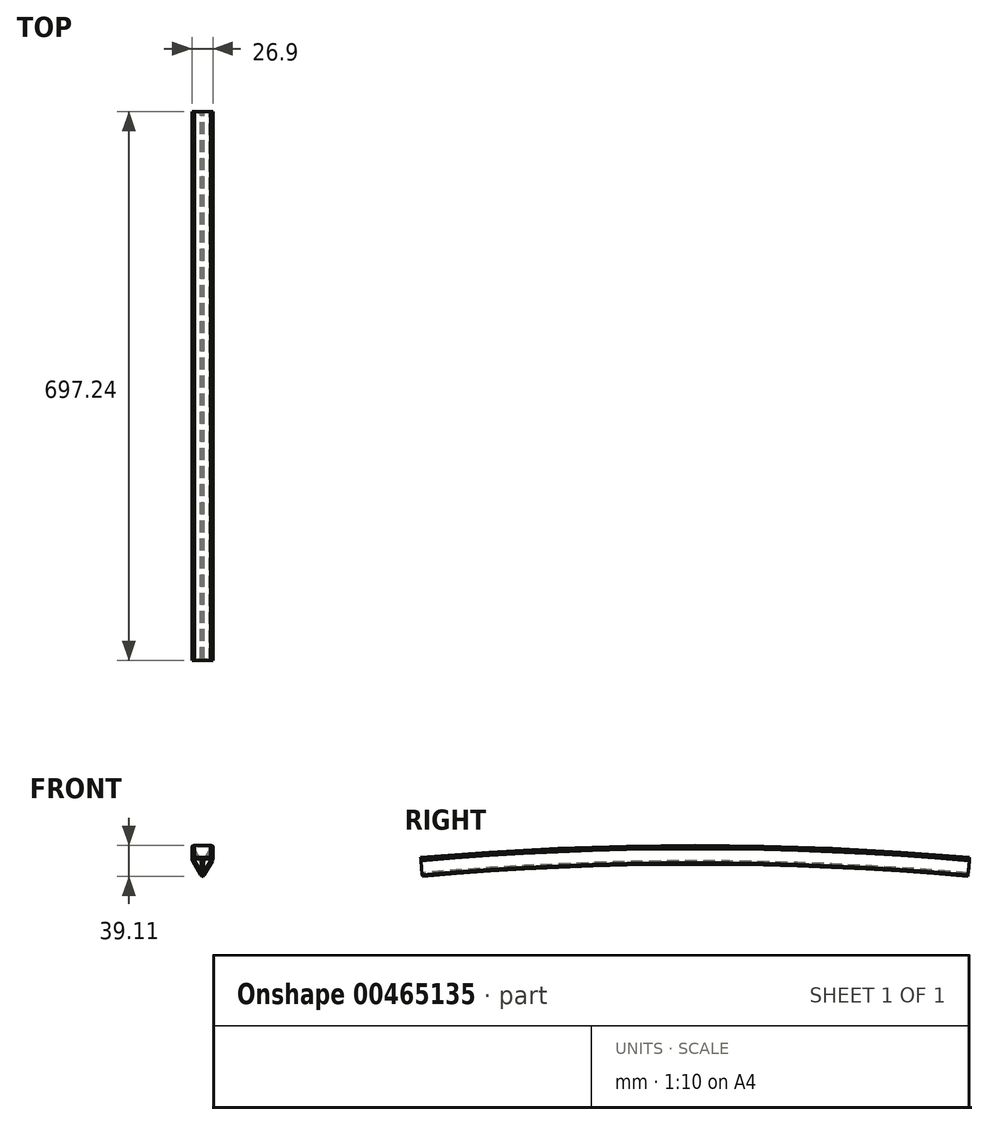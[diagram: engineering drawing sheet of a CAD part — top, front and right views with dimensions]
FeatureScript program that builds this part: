
annotation { "Feature Type Name" : "Feature", "Feature Type Description" : "" }
export const myFeature = defineFeature(function(context is Context, id is Id, definition is map)
    precondition{}
    {
        {
            var Q0;
            Q0=qCreatedBy(makeId("Front.planeOp"),FACE);
            var sketch = newSketch(context, id + "F0", { "sketchPlane" : qUnion([Q0])});
            skLineSegment(sketch, "E0", {"start": v(-10.27, 9) * mm, "end": v(10.27, 9) * mm});
            skLineSegment(sketch, "E1", {"start": v(12.63, 4.9) * mm, "end": v(2.37, -12.88) * mm});
            skLineSegment(sketch, "E2", {"start": v(-2.37, -12.88) * mm, "end": v(-12.63, 4.9) * mm});
            skPoint(sketch, "E3", {"position": v(0, 9) * mm});
            skPoint(sketch, "E4", {"position": v(7.5, -4) * mm});
            skPoint(sketch, "E5", {"position": v(-7.5, -4) * mm});
            skLineSegment(sketch, "E6", {"start": v(0, -14.98) * mm, "end": v(0.68, -14.8) * mm});
            skPoint(sketch, "E7", {"position": v(0.68, -14.8) * mm});
            skLineSegment(sketch, "E8", {"start": v(0.68, -14.8) * mm, "end": v(1.2, -14.4) * mm});
            skPoint(sketch, "E9", {"position": v(1.2, -14.4) * mm});
            skLineSegment(sketch, "E10", {"start": v(1.2, -14.4) * mm, "end": v(1.62, -13.92) * mm});
            skPoint(sketch, "E11", {"position": v(1.62, -13.92) * mm});
            skLineSegment(sketch, "E12", {"start": v(1.62, -13.92) * mm, "end": v(2.37, -12.88) * mm});
            skLineSegment(sketch, "E13.MirrorCS", {"start": v(-0.68, -14.8) * mm, "end": v(-1.2, -14.4) * mm});
            skLineSegment(sketch, "E14.MirrorCS", {"start": v(-1.2, -14.4) * mm, "end": v(-1.62, -13.92) * mm});
            skLineSegment(sketch, "E15.MirrorCS", {"start": v(-1.62, -13.92) * mm, "end": v(-2.37, -12.88) * mm});
            skLineSegment(sketch, "E16.MirrorCS", {"start": v(0, -14.98) * mm, "end": v(-0.68, -14.8) * mm});
            skLineSegment(sketch, "E17.MirrorCS", {"start": v(13.45, 7.32) * mm, "end": v(13.37, 6.67) * mm});
            skLineSegment(sketch, "E18.MirrorCS", {"start": v(13.27, 8) * mm, "end": v(13.45, 7.32) * mm});
            skLineSegment(sketch, "E19.MirrorCS", {"start": v(13.37, 6.67) * mm, "end": v(13.16, 6.06) * mm});
            skLineSegment(sketch, "E20.MirrorCS", {"start": v(13.16, 6.06) * mm, "end": v(12.63, 4.9) * mm});
            skLineSegment(sketch, "E21.MirrorCS", {"start": v(13.27, 8) * mm, "end": v(12.77, 8.5) * mm});
            skLineSegment(sketch, "E22.MirrorCS", {"start": v(12.16, 8.75) * mm, "end": v(11.54, 8.88) * mm});
            skLineSegment(sketch, "E23.MirrorCS", {"start": v(11.54, 8.88) * mm, "end": v(10.27, 9) * mm});
            skLineSegment(sketch, "E24.MirrorCS", {"start": v(12.77, 8.5) * mm, "end": v(12.16, 8.75) * mm});
            skLineSegment(sketch, "E25.MirrorCS", {"start": v(-12.77, 8.5) * mm, "end": v(-12.16, 8.75) * mm});
            skLineSegment(sketch, "E26.MirrorCS", {"start": v(-13.27, 8) * mm, "end": v(-12.77, 8.5) * mm});
            skLineSegment(sketch, "E27.MirrorCS", {"start": v(-11.54, 8.88) * mm, "end": v(-10.27, 9) * mm});
            skLineSegment(sketch, "E28.MirrorCS", {"start": v(-12.16, 8.75) * mm, "end": v(-11.54, 8.87) * mm});
            skLineSegment(sketch, "E29.MirrorCS", {"start": v(-13.27, 8) * mm, "end": v(-13.45, 7.32) * mm});
            skLineSegment(sketch, "E30.MirrorCS", {"start": v(-13.37, 6.67) * mm, "end": v(-13.16, 6.06) * mm});
            skLineSegment(sketch, "E31.MirrorCS", {"start": v(-13.45, 7.32) * mm, "end": v(-13.37, 6.67) * mm});
            skLineSegment(sketch, "E32.MirrorCS", {"start": v(-13.16, 6.06) * mm, "end": v(-12.63, 4.9) * mm});
            skPoint(sketch, "E33.orphan", {"position": v(-15, 9) * mm});
            skPoint(sketch, "E34.orphan", {"position": v(-12.27, 9) * mm});
            skPoint(sketch, "E35.orphan", {"position": v(-11.56, 9) * mm});
            skPoint(sketch, "E36.orphan", {"position": v(-10.9, 9) * mm});
            skPoint(sketch, "E37.orphan", {"position": v(-13.63, 6.63) * mm});
            skPoint(sketch, "E38.orphan", {"position": v(-13.28, 6.02) * mm});
            skPoint(sketch, "E39.orphan", {"position": v(-12.95, 5.46) * mm});
            skPoint(sketch, "E40.orphan", {"position": v(15, 9) * mm});
            skPoint(sketch, "E41.orphan", {"position": v(12.27, 9) * mm});
            skPoint(sketch, "E42.orphan", {"position": v(11.56, 9) * mm});
            skPoint(sketch, "E43.orphan", {"position": v(10.9, 9) * mm});
            skPoint(sketch, "E44.orphan", {"position": v(13.63, 6.63) * mm});
            skPoint(sketch, "E45.orphan", {"position": v(13.28, 6.02) * mm});
            skPoint(sketch, "E46.orphan", {"position": v(12.95, 5.46) * mm});
            skPoint(sketch, "E47.orphan", {"position": v(0, -16.98) * mm});
            skPoint(sketch, "E48.orphan", {"position": v(-1.37, -14.61) * mm});
            skPoint(sketch, "E49.orphan", {"position": v(-1.72, -14) * mm});
            skPoint(sketch, "E50.orphan", {"position": v(1.37, -14.61) * mm});
            skPoint(sketch, "E51.orphan", {"position": v(1.72, -14) * mm});
            skPoint(sketch, "E52.orphan", {"position": v(2.05, -13.44) * mm});
            skPoint(sketch, "E53.orphan", {"position": v(-2.05, -13.44) * mm});
            skLineSegment(sketch, "E54", {"start": v(-8.33, -3991) * mm, "end": v(15.82, -3991) * mm});
            skLineSegment(sketch, "E55", {"start": v(-5.77, -3) * mm, "end": v(10.54, 6.42) * mm});
            skLineSegment(sketch, "E56", {"start": v(5.77, -3) * mm, "end": v(-10.54, 6.42) * mm});
            skLineSegment(sketch, "E57", {"start": v(0, 9) * mm, "end": v(0, -11.83) * mm});
            skLineSegment(sketch, "E58", {"start": v(-8.8, 7) * mm, "end": v(8.8, 7) * mm});
            skLineSegment(sketch, "E59", {"start": v(10.17, 4.63) * mm, "end": v(1.37, -10.61) * mm});
            skLineSegment(sketch, "E60", {"start": v(-10.17, 4.63) * mm, "end": v(-1.37, -10.61) * mm});
            skLineSegment(sketch, "E61", {"start": v(-10.54, 6.42) * mm, "end": v(-10.25, 6.71) * mm});
            skPoint(sketch, "E62", {"position": v(-10.25, 6.71) * mm});
            skLineSegment(sketch, "E63", {"start": v(-10.25, 6.71) * mm, "end": v(-9.9, 6.86) * mm});
            skPoint(sketch, "E64", {"position": v(-9.9, 6.86) * mm});
            skLineSegment(sketch, "E65", {"start": v(-9.9, 6.86) * mm, "end": v(-9.54, 6.93) * mm});
            skPoint(sketch, "E66", {"position": v(-9.54, 6.93) * mm});
            skLineSegment(sketch, "E67", {"start": v(-9.54, 6.93) * mm, "end": v(-8.8, 7) * mm});
            skLineSegment(sketch, "E68.MirrorCS", {"start": v(-10.64, 6.03) * mm, "end": v(-10.6, 5.65) * mm});
            skLineSegment(sketch, "E69.MirrorCS", {"start": v(-10.47, 5.3) * mm, "end": v(-10.17, 4.63) * mm});
            skLineSegment(sketch, "E70.MirrorCS", {"start": v(-10.54, 6.42) * mm, "end": v(-10.64, 6.03) * mm});
            skLineSegment(sketch, "E71.MirrorCS", {"start": v(-10.6, 5.65) * mm, "end": v(-10.47, 5.3) * mm});
            skLineSegment(sketch, "E72.MirrorCS", {"start": v(10.25, 6.71) * mm, "end": v(9.9, 6.86) * mm});
            skLineSegment(sketch, "E73.MirrorCS", {"start": v(9.54, 6.93) * mm, "end": v(8.8, 7) * mm});
            skLineSegment(sketch, "E74.MirrorCS", {"start": v(10.54, 6.42) * mm, "end": v(10.25, 6.71) * mm});
            skLineSegment(sketch, "E75.MirrorCS", {"start": v(9.9, 6.86) * mm, "end": v(9.54, 6.93) * mm});
            skLineSegment(sketch, "E76.MirrorCS", {"start": v(10.6, 5.65) * mm, "end": v(10.47, 5.3) * mm});
            skLineSegment(sketch, "E77.MirrorCS", {"start": v(10.64, 6.03) * mm, "end": v(10.6, 5.65) * mm});
            skLineSegment(sketch, "E78.MirrorCS", {"start": v(10.54, 6.42) * mm, "end": v(10.64, 6.03) * mm});
            skLineSegment(sketch, "E79.MirrorCS", {"start": v(10.47, 5.3) * mm, "end": v(10.17, 4.63) * mm});
            skLineSegment(sketch, "E80.MirrorCS", {"start": v(0, -11.83) * mm, "end": v(0.4, -11.72) * mm});
            skLineSegment(sketch, "E81.MirrorCS", {"start": v(0.4, -11.72) * mm, "end": v(0.7, -11.5) * mm});
            skLineSegment(sketch, "E82.MirrorCS", {"start": v(0.94, -11.21) * mm, "end": v(1.37, -10.61) * mm});
            skLineSegment(sketch, "E83.MirrorCS", {"start": v(0.7, -11.5) * mm, "end": v(0.94, -11.21) * mm});
            skLineSegment(sketch, "E84.MirrorCS", {"start": v(0, -11.83) * mm, "end": v(-0.4, -11.72) * mm});
            skLineSegment(sketch, "E85.MirrorCS", {"start": v(-0.94, -11.21) * mm, "end": v(-1.37, -10.61) * mm});
            skLineSegment(sketch, "E86.MirrorCS", {"start": v(-0.7, -11.5) * mm, "end": v(-0.94, -11.21) * mm});
            skLineSegment(sketch, "E87.MirrorCS", {"start": v(-0.4, -11.72) * mm, "end": v(-0.7, -11.5) * mm});
            skPoint(sketch, "E88.orphan", {"position": v(9.17, 7) * mm});
            skPoint(sketch, "E89.orphan", {"position": v(9.55, 7) * mm});
            skPoint(sketch, "E90.orphan", {"position": v(10.54, 5.28) * mm});
            skPoint(sketch, "E91.orphan", {"position": v(10.35, 4.95) * mm});
            skPoint(sketch, "E92.orphan", {"position": v(9.96, 7) * mm});
            skPoint(sketch, "E93.orphan", {"position": v(10.75, 5.63) * mm});
            skPoint(sketch, "E94.orphan", {"position": v(-10.35, 4.95) * mm});
            skPoint(sketch, "E95.orphan", {"position": v(-10.54, 5.28) * mm});
            skPoint(sketch, "E96.orphan", {"position": v(-10.75, 5.63) * mm});
            skPoint(sketch, "E97.orphan", {"position": v(-9.96, 7) * mm});
            skPoint(sketch, "E98.orphan", {"position": v(-9.55, 7) * mm});
            skPoint(sketch, "E99.orphan", {"position": v(-9.17, 7) * mm});
            skPoint(sketch, "E100.orphan", {"position": v(-1.18, -10.93) * mm});
            skPoint(sketch, "E101.orphan", {"position": v(-1, -11.26) * mm});
            skPoint(sketch, "E102.orphan", {"position": v(-0.79, -11.61) * mm});
            skPoint(sketch, "E103.orphan", {"position": v(1, -11.26) * mm});
            skPoint(sketch, "E104.orphan", {"position": v(0.79, -11.61) * mm});
            skPoint(sketch, "E105.orphan", {"position": v(1.18, -10.93) * mm});
            skPoint(sketch, "E106", {"position": v(13.45, 7.32) * mm});
            skSolve(sketch);
        }
        {
            var Q0;
            Q0=makeQuery(id+"F0.imprint","IMPRINT",FACE,{"disambiguationData":[TD([[makeQuery(id+"F0.imprint","IMPRINT",EDGE,{"derivedFrom":sQuery(id+"F0.wireOp",EDGE,"E1")}),-1.0]])]});
            var Q1;
            Q1=sQuery(id+"F0.wireOp",EDGE,"E54");
            revolve(context, id + "F1", {"entities" : qUnion([Q0]), "axis" : qUnion([Q1]), "revolveType" : RevolveType.SYMMETRIC, "angle" : 10 * degree});
        }
    });
